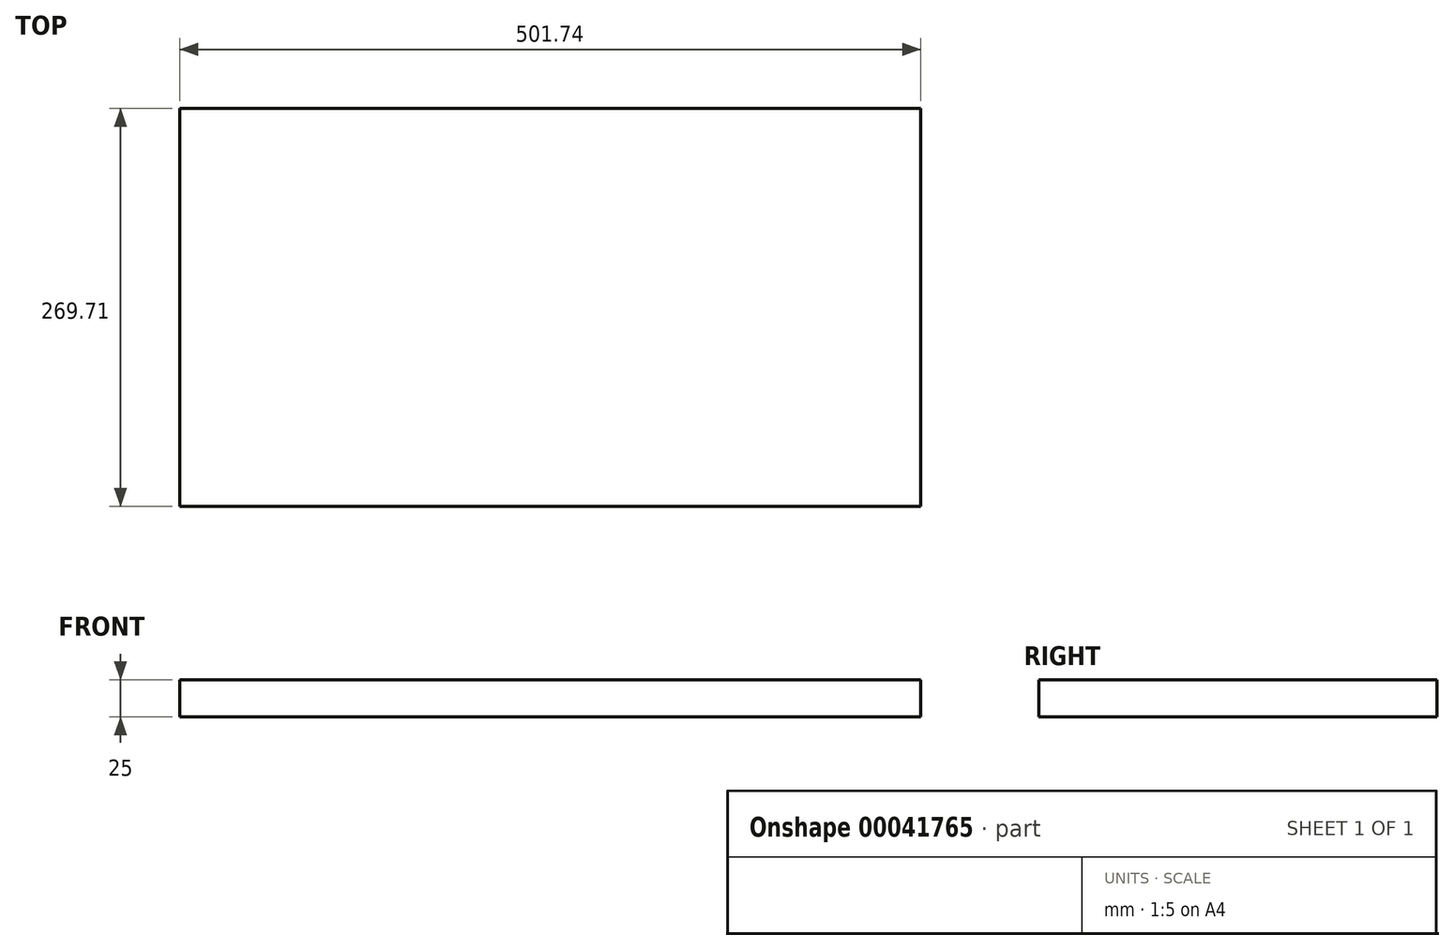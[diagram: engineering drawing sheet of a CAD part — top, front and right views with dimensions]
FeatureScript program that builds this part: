
annotation { "Feature Type Name" : "Feature", "Feature Type Description" : "" }
export const myFeature = defineFeature(function(context is Context, id is Id, definition is map)
    precondition{}
    {
        {
            var Q0;
            Q0=qCreatedBy(makeId("Top.planeOp"),FACE);
            var sketch = newSketch(context, id + "F0", { "sketchPlane" : qUnion([Q0])});
            skLineSegment(sketch, "E0.bottom", {"start": v(-253.23, 112.2) * mm, "end": v(248.51, 112.2) * mm});
            skLineSegment(sketch, "E0.top", {"start": v(-253.23, -157.51) * mm, "end": v(248.51, -157.51) * mm});
            skLineSegment(sketch, "E0.left", {"start": v(-253.23, 112.2) * mm, "end": v(-253.23, -157.51) * mm});
            skLineSegment(sketch, "E0.right", {"start": v(248.51, 112.2) * mm, "end": v(248.51, -157.51) * mm});
            skSolve(sketch);
        }
        {
            var Q0;
            Q0=makeQuery(id+"F0.imprint","IMPRINT",FACE,{"disambiguationData":[TD([[makeQuery(id+"F0.imprint","IMPRINT",EDGE,{"derivedFrom":sQuery(id+"F0.wireOp",EDGE,"E0.bottom")}),-1.0]])]});
            extrude(context, id + "F1", {"entities" : qUnion([Q0]), "depth" : 25 * mm});
        }
    });
